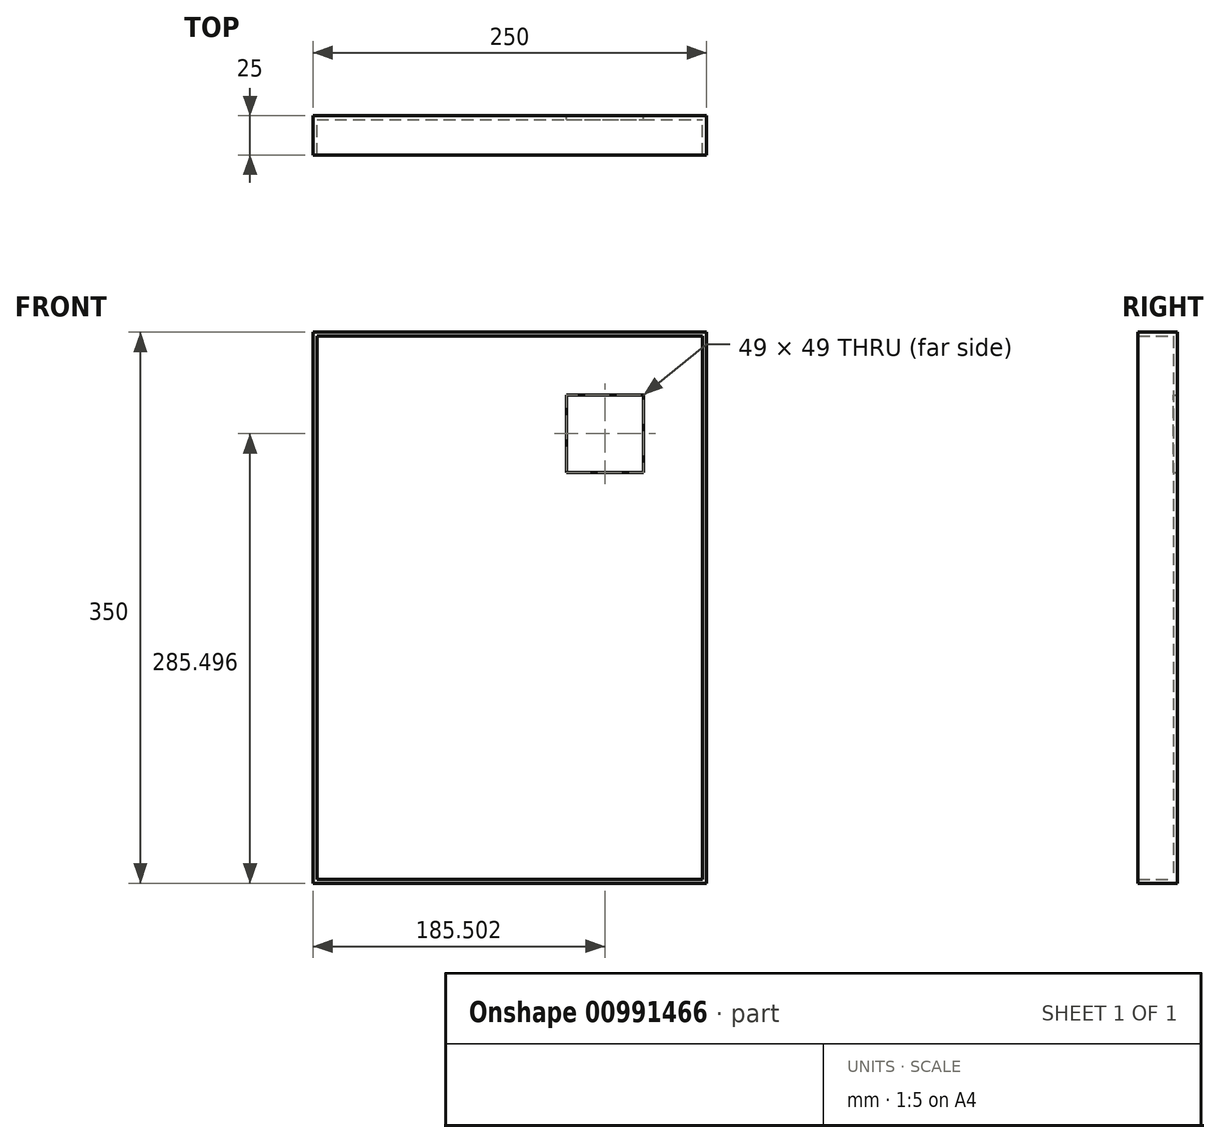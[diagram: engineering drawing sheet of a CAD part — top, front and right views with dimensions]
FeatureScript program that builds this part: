
annotation { "Feature Type Name" : "Feature", "Feature Type Description" : "" }
export const myFeature = defineFeature(function(context is Context, id is Id, definition is map)
    precondition{}
    {
        {
            var Q0;
            Q0=qCreatedBy(makeId("Front.planeOp"),FACE);
            var sketch = newSketch(context, id + "F0", { "sketchPlane" : qUnion([Q0])});
            skLineSegment(sketch, "E0.bottom", {"start": v(-55.26, 295.1) * mm, "end": v(194.74, 295.1) * mm});
            skLineSegment(sketch, "E0.top", {"start": v(-55.26, -54.9) * mm, "end": v(194.74, -54.9) * mm});
            skLineSegment(sketch, "E0.left", {"start": v(-55.26, 295.1) * mm, "end": v(-55.26, -54.9) * mm});
            skLineSegment(sketch, "E0.right", {"start": v(194.74, 295.1) * mm, "end": v(194.74, -54.9) * mm});
            skSolve(sketch);
        }
        {
            var Q0;
            Q0=qSketchRegion(id+"F0",true);
            extrude(context, id + "F1", {"entities" : qUnion([Q0]), "depth" : 25 * mm, "offsetDistance" : 25 * mm});
        }
        {
            var Q0;
            Q0=makeQuery(id+"F1.opExtrude","CAP_FACE",FACE,{"disambiguationData":[OSD([sQuery(id+"F0.wireOp",EDGE,"E0.bottom"),sQuery(id+"F0.wireOp",EDGE,"E0.top"),sQuery(id+"F0.wireOp",EDGE,"E0.left"),sQuery(id+"F0.wireOp",EDGE,"E0.right")])],"isStart":false});
            shell(context, id + "F2", {"entities" : qUnion([Q0]), "thickness" : 2.5 * mm});
        }
        {
            var Q0;
            Q0=makeQuery(id+"F0.imprint","IMPRINT",FACE,{"disambiguationData":[TD([[makeQuery(id+"F0.imprint","IMPRINT",EDGE,{"derivedFrom":sQuery(id+"F0.wireOp",EDGE,"E0.bottom")}),-1.0]])]});
            var sketch = newSketch(context, id + "F3", { "sketchPlane" : qUnion([Q0])});
            skLineSegment(sketch, "E1.bottom", {"start": v(154.74, 255.1) * mm, "end": v(105.74, 255.1) * mm});
            skLineSegment(sketch, "E1.top", {"start": v(154.74, 206.1) * mm, "end": v(105.74, 206.1) * mm});
            skLineSegment(sketch, "E1.left", {"start": v(154.74, 255.1) * mm, "end": v(154.74, 206.1) * mm});
            skLineSegment(sketch, "E1.right", {"start": v(105.74, 255.1) * mm, "end": v(105.74, 206.1) * mm});
            skSolve(sketch);
        }
        {
            var Q0;
            Q0=makeQuery(id+"F3.imprint","IMPRINT",FACE,{"disambiguationData":[TD([[makeQuery(id+"F3.imprint","IMPRINT",EDGE,{"derivedFrom":sQuery(id+"F3.wireOp",EDGE,"E1.bottom")}),1.0]])]});
            extrude(context, id + "F4", {"entities" : qUnion([Q0]), "operationType" : NewBodyOperationType.REMOVE, "depth" : 25 * mm, "offsetDistance" : 25 * mm});
        }
    });
